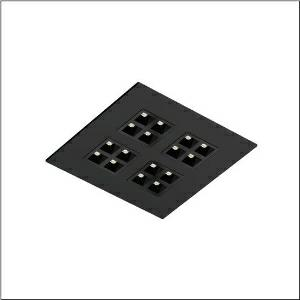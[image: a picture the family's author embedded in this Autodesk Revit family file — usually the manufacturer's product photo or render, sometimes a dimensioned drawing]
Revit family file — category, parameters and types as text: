
# Revit family: silica_r__31_square_51my6ldu44ba_f66e
name_source: partatom
category: Lighting Fixtures
units: mm (PartAtom-declared; Revit-internal decimal feet)

## family parameters
Cut with Voids When Loaded = No
Host = Face
Light Source = No
Part Type = Normal
Room Calculation Point = No
Round Connector Dimension = Use Diameter
Shared = No

## types (1)
- --- (1 x LED, 6310 lm, 38.5 W, 4000K)
    Apparent Load = 39 VA
    CIE Flux Codes = 82 100 100 100 100
    Color Rendering = 80
    Color Temperature = 4000K
    Default Elevation = 1800 mm
    Description = Silica® 31 Square, office luminaire, primary light control with lens, of PMMA, primary anti-glare with reflector, of PC, black, light emission: direct distribution, primary light characteristic: symmetric, installation type: lay-in mounting, LED, rated luminous flux: 4.620lm, luminous efficacy: 167lm/W, light colour: 840, colour temperature: 4000K, control gear: DALI 2, Multilumen, with terminal, 5-pole, mains connection: 220..240V, AC, 50/60Hz, rated input power: 27.6W, luminaire housing, of sheet steel, coated, jet black (RAL 9005), module: M625, length: 620mm, width: 620mm, height: 43mm, protection rating (complete): IP20, insulation class (complete): insulation class II (safety insulation), certification: CE, impact resistance: IK03, permissible operating ambient temperature: -20..+35°C, standard: EN 50419, packaging unit: 1 piece
    Height = 0 mm  [stored 0 ft]
    Lamp = 1 x LED
    Lamp Light Flux = 6310 lm
    Lamp Power = 38.5 W
    Lamp count = 1
    Length = 620 mm
    Luminous efficacy = 164 lm/W
    Manufacturer = Siteco
    ModVariant = No
    Model = 51MY6LDU44BA
    Mounting Place = Ceiling
    Mounting Type = Recessed
    Number of Poles = 1
    OnlyDefault = Yes
    Power Factor = 1
    Product Name = Silica® 31 Square
    Product group = office luminaire | ceiling recessed
    ProductGroupID = 401
    Protection Class = Protection class II
    Protection Degree = IP 20
    RLX_Detail_Level = 1
    RLX_Emergency_Light_Flux = 0 lm
    RLX_Emergency_Type = 0
    RLX_Emergency_Type_DB = No
    RlxData = <blob elided: 35525 chars, md5=e836e492>
    Socket = socket
    Standby Power = 0 W
    System Light Flux = 6310 lm
    System Power = 39 W
    Type Comments = factory setting: luminous flux: 100 % | (OFF | OFF | OFF | OFF) | 1050 mA
    Type Image = l_1313660.jpg
    URL = http://relux.com
    VarID = @adj_036276
    Voltage = 0 V
    Weight = 0.00 kg
    Width = 620 mm

note: [stored X ft] marks values corroborated as IEEE doubles in the binary element streams (Revit-internal decimal feet)

## geometry (parser evidence)
native form markers: Blend x4, Sweep x11
no freeform markers — native parametric forms only
